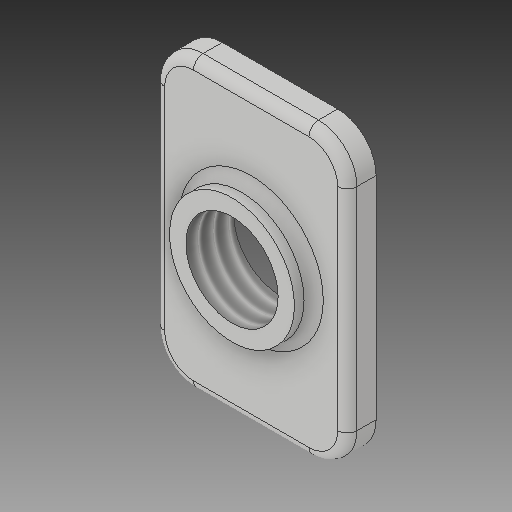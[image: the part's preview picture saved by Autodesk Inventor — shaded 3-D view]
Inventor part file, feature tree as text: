
AUTODESK INVENTOR PART (.ipt)
format: ipt  version: 2018 (Build 220112000, 112)  size: 178,176 bytes
history: native  units: mm
features: other x3, sketch x2
ambient origin geometry x8: Origin, YZ Plane, XZ Plane, XY Plane, X Axis, Y Axis, Z Axis, Center Point
bodies: Solid1 (feature_tree)
feature tree (5):
  other  "M5 Tee Nut-Generic_MIR_CPY_MIR_MIR.ipt"
  other  "Solid1::M5 Tee Nut-Generic_MIR_CPY_MIR_MIR.ipt"
  other  "TaggingFeature1"
  sketch  "Sketch1"  dims[d0=10.0mm]
  sketch  "Sketch2"
